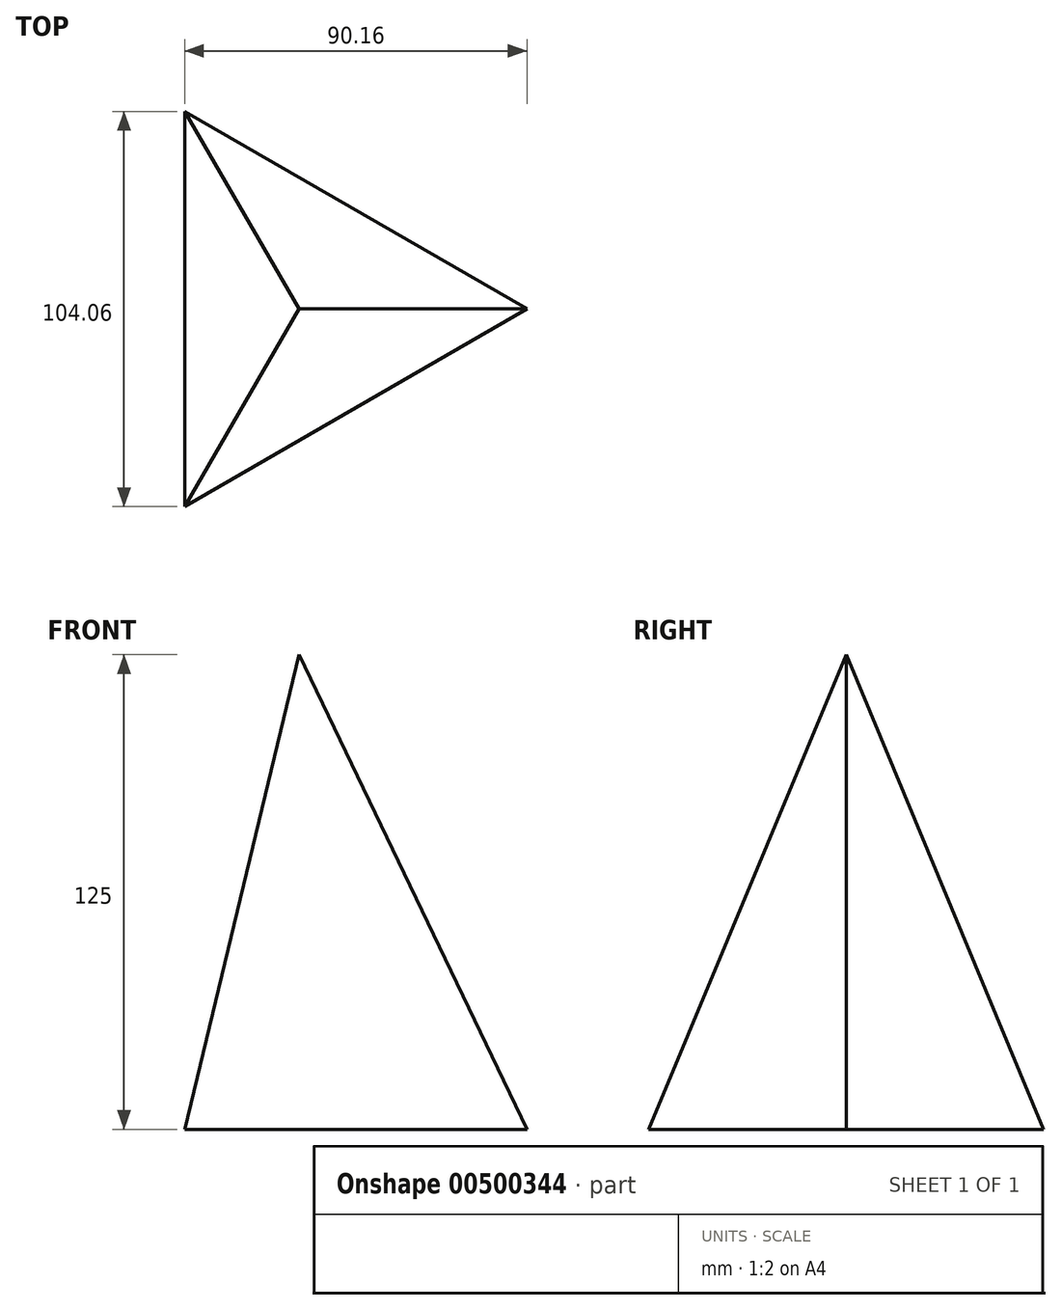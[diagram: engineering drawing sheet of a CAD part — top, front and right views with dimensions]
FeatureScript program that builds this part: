
annotation { "Feature Type Name" : "Feature", "Feature Type Description" : "" }
export const myFeature = defineFeature(function(context is Context, id is Id, definition is map)
    precondition{}
    {
        {
            var Q0;
            Q0=qCreatedBy(makeId("Top.planeOp"),FACE);
            var sketch = newSketch(context, id + "F0", { "sketchPlane" : qUnion([Q0])});
            skCircle(sketch, "E0.cCircle", {"center": v(0, 0) * mm, "radius": 60.08 * mm, "construction": true});
            skLineSegment(sketch, "E0.0", {"start": v(-30, -52.05) * mm, "end": v(-30.08, 52) * mm});
            skLineSegment(sketch, "E0.1", {"start": v(-30.08, 52) * mm, "end": v(60.08, 0.04) * mm});
            skLineSegment(sketch, "E0.2", {"start": v(60.08, 0.04) * mm, "end": v(-30, -52.05) * mm});
            skSolve(sketch);
        }
        {
            var Q0;
            Q0=qCreatedBy(makeId("Top.planeOp"),FACE);
            cPlane(context, id + "F1", {"entities" : qUnion([Q0]), "cplaneType" : CPlaneType.OFFSET, "offset" : 125 * mm, "width" : 150 * mm, "height" : 150 * mm});
        }
        {
            var Q0;
            Q0=qCreatedBy(id+"F1.planeOp",FACE);
            var sketch = newSketch(context, id + "F2", { "sketchPlane" : qUnion([Q0])});
            skPoint(sketch, "E1", {"position": v(0, 0) * mm});
            skSolve(sketch);
        }
        {
            var Q0;
            Q0=makeQuery(id+"F0.imprint","IMPRINT",FACE,{"disambiguationData":[TD([[makeQuery(id+"F0.imprint","IMPRINT",EDGE,{"derivedFrom":sQuery(id+"F0.wireOp",EDGE,"E0.0")}),-1.0]])]});
            var Q1;
            Q1=sQuery(id+"F2.wireOp",VERTEX,"E1");
            loft(context, id + "F3", {"sheetProfilesArray" : [{ "sheetProfileEntities" : qUnion([Q0]) }, { "sheetProfileEntities" : qUnion([Q1]) }]});
        }
    });
